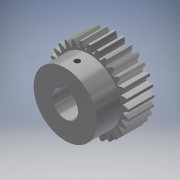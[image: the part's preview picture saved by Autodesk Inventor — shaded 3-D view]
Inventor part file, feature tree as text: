
AUTODESK INVENTOR PART (.ipt)
format: ipt  version: 2019 (Build 230136000, 136)  size: 307,200 bytes
history: native  units: mm (DEFAULTED — no unit token found)
features: sketch x5, plane x4, extrude x3, other x3, hole x1, projected_geometry x1
ambient origin geometry x8: Origin, YZ Plane, XZ Plane, XY Plane, X Axis, Y Axis, Z Axis, Center Point
bodies: Solid1 (feature_tree)
feature tree (17):
  extrude  "Extrusion1"  Depth=15.0mm TaperAngle=0.0deg
  plane  "Work Plane2"
  plane  "Work Plane8"
  plane  "Work Plane9"
  other  "正齒輪"
  extrude  "擠出2"  Depth=10.0mm TaperAngle=0.0deg
  extrude  "擠出3"  Depth=29.0mm
  plane  "工作平面11"
  hole  "孔1"  [1 undecoded]
  sketch  "Sketch1"  dims[d0=46.466966mm d1=15.0mm d2=0.0mm]
  sketch  "Sketch2"  dims[d3=43.889556mm d4=10.0mm d5=0.0mm d16=56.753736mm d17=0.0mm d34=1.083308mm d39=0.0mm d41=0.0mm d43=56.753736mm d46=56.753736mm d47=0.0mm d48=0.0mm d49=15.0mm d50=29.0mm d51=0.0mm d52=37.0mm d53=2.0mm d54=5.0mm d55=2.0mm d56=14.0mm d57=0.0mm d58=3.242mm d59=8.0mm d60=4.0mm d61=2.0mm d62=90.0deg d63=8.0mm d64=20.594885mm d65=5.833761mm]
  other  "Srf1"
  sketch  "草圖3"
  sketch  "草圖4"
  sketch  "草圖5"
  projected_geometry  "投影迴路1"
  other  "節圓直徑"
note: 1 required parameter value undecoded (feature->parameter linkage not recoverable at this tier; creation-order binding heuristic only, values carry confidence <= 0.55)
